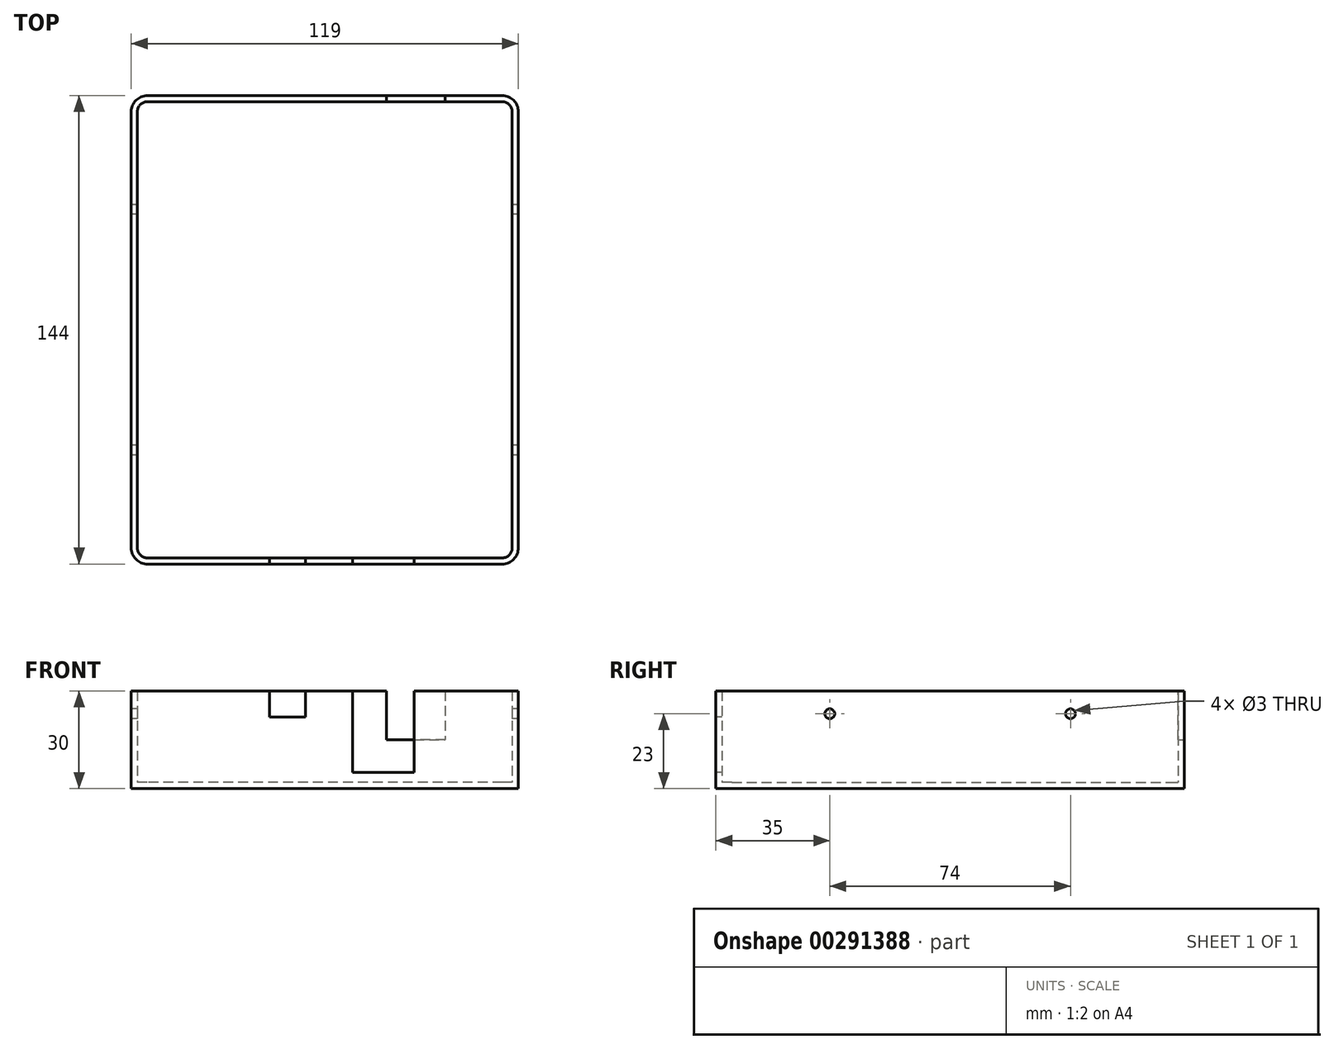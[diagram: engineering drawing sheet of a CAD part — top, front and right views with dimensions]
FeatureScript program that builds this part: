
annotation { "Feature Type Name" : "Feature", "Feature Type Description" : "" }
export const myFeature = defineFeature(function(context is Context, id is Id, definition is map)
    precondition{}
    {
        {
            var Q0;
            Q0=qCreatedBy(makeId("Top.planeOp"),FACE);
            var sketch = newSketch(context, id + "F0", { "sketchPlane" : qUnion([Q0])});
            skLineSegment(sketch, "E0.bottom", {"start": v(59.5, -72) * mm, "end": v(-59.5, -72) * mm});
            skLineSegment(sketch, "E0.top", {"start": v(59.5, 72) * mm, "end": v(-59.5, 72) * mm});
            skLineSegment(sketch, "E0.left", {"start": v(59.5, -72) * mm, "end": v(59.5, 72) * mm});
            skLineSegment(sketch, "E0.right", {"start": v(-59.5, -72) * mm, "end": v(-59.5, 72) * mm});
            skPoint(sketch, "E0.middle", {"position": v(0, 0) * mm});
            skSolve(sketch);
        }
        {
            var Q0;
            Q0 = qSketchRegion(id + "F0", true);
            extrude(context, id + "F1", {"entities" : qUnion([Q0]), "depth" : 30 * mm});
        }
        {
            var Q0;
            Q0=makeQuery(id+"F1.opExtrude","CAP_FACE",FACE,{"disambiguationData":[OSD([sQuery(id+"F0.wireOp",EDGE,"E0.bottom"),sQuery(id+"F0.wireOp",EDGE,"E0.top"),sQuery(id+"F0.wireOp",EDGE,"E0.left"),sQuery(id+"F0.wireOp",EDGE,"E0.right")])],"isStart":false});
            shell(context, id + "F2", {"entities" : qUnion([Q0]), "thickness" : 1.9 * mm});
        }
        {
            var Q0;
            Q0=makeQuery(id+"F1.opExtrude","SWEPT_EDGE",EDGE,{"disambiguationData":[OSD([sQuery(id+"F0.wireOp",EDGE,"E0.bottom"),sQuery(id+"F0.wireOp",EDGE,"E0.right")])]});
            var Q1;
            Q1=makeQuery(id+"F1.opExtrude","SWEPT_EDGE",EDGE,{"disambiguationData":[OSD([sQuery(id+"F0.wireOp",EDGE,"E0.bottom"),sQuery(id+"F0.wireOp",EDGE,"E0.left")])]});
            var Q2;
            Q2=makeQuery(id+"F1.opExtrude","SWEPT_EDGE",EDGE,{"disambiguationData":[OSD([sQuery(id+"F0.wireOp",EDGE,"E0.top"),sQuery(id+"F0.wireOp",EDGE,"E0.left")])]});
            var Q3;
            Q3=makeQuery(id+"F1.opExtrude","SWEPT_EDGE",EDGE,{"disambiguationData":[OSD([sQuery(id+"F0.wireOp",EDGE,"E0.top"),sQuery(id+"F0.wireOp",EDGE,"E0.right")])]});
            fillet(context, id + "F3", {"entities" : qUnion([Q0, Q1, Q2, Q3]), "radius" : 5 * mm, "tangentPropagation" : true, "allowEdgeOverflow" : false});
        }
        {
            var Q0;
            Q0=makeQuery(id+"F2.opShell","OFFSET_EDGE",EDGE,{"disambiguationData":[OSD([sQuery(id+"F0.wireOp",EDGE,"E0.bottom"),sQuery(id+"F0.wireOp",EDGE,"E0.right")])]});
            var Q1;
            Q1=makeQuery(id+"F2.opShell","OFFSET_EDGE",EDGE,{"disambiguationData":[OSD([sQuery(id+"F0.wireOp",EDGE,"E0.bottom"),sQuery(id+"F0.wireOp",EDGE,"E0.left")])]});
            var Q2;
            Q2=makeQuery(id+"F2.opShell","OFFSET_EDGE",EDGE,{"disambiguationData":[OSD([sQuery(id+"F0.wireOp",EDGE,"E0.top"),sQuery(id+"F0.wireOp",EDGE,"E0.right")])]});
            var Q3;
            Q3=makeQuery(id+"F2.opShell","OFFSET_EDGE",EDGE,{"disambiguationData":[OSD([sQuery(id+"F0.wireOp",EDGE,"E0.top"),sQuery(id+"F0.wireOp",EDGE,"E0.left")])]});
            fillet(context, id + "F4", {"entities" : qUnion([Q0, Q1, Q2, Q3]), "radius" : 3 * mm, "tangentPropagation" : true, "allowEdgeOverflow" : false});
        }
        {
            var Q0;
            Q0=makeQuery(id+"F1.opExtrude","SWEPT_FACE",FACE,{"disambiguationData":[OSD([sQuery(id+"F0.wireOp",EDGE,"E0.right")])]});
            var sketch = newSketch(context, id + "F5", { "sketchPlane" : qUnion([Q0])});
            skCircle(sketch, "E1", {"center": v(-37, 23) * mm, "radius": 1.5 * mm});
            skCircle(sketch, "E2", {"center": v(37, 23) * mm, "radius": 1.5 * mm});
            skSolve(sketch);
        }
        {
            var Q0;
            Q0 = qSketchRegion(id + "F5", true);
            extrude(context, id + "F6", {"entities" : qUnion([Q0]), "operationType" : NewBodyOperationType.REMOVE, "endBound" : BoundingType.THROUGH_ALL, "oppositeDirection" : true, "depth" : 25 * mm});
        }
        {
            var Q0;
            Q0=makeQuery(id+"F1.opExtrude","SWEPT_FACE",FACE,{"disambiguationData":[OSD([sQuery(id+"F0.wireOp",EDGE,"E0.bottom")])]});
            var sketch = newSketch(context, id + "F7", { "sketchPlane" : qUnion([Q0])});
            skLineSegment(sketch, "E3.bottom", {"start": v(8.5, 30) * mm, "end": v(27.5, 30) * mm});
            skLineSegment(sketch, "E3.top", {"start": v(8.5, 5) * mm, "end": v(27.5, 5) * mm});
            skLineSegment(sketch, "E3.left", {"start": v(8.5, 30) * mm, "end": v(8.5, 5) * mm});
            skLineSegment(sketch, "E3.right", {"start": v(27.5, 30) * mm, "end": v(27.5, 5) * mm});
            skLineSegment(sketch, "E4.bottom", {"start": v(-17, 30) * mm, "end": v(-6, 30) * mm});
            skLineSegment(sketch, "E4.top", {"start": v(-17, 22) * mm, "end": v(-6, 22) * mm});
            skLineSegment(sketch, "E4.left", {"start": v(-17, 30) * mm, "end": v(-17, 22) * mm});
            skLineSegment(sketch, "E4.right", {"start": v(-6, 30) * mm, "end": v(-6, 22) * mm});
            skSolve(sketch);
        }
        {
            var Q0;
            Q0 = qSketchRegion(id + "F7", true);
            extrude(context, id + "F8", {"entities" : qUnion([Q0]), "operationType" : NewBodyOperationType.REMOVE, "oppositeDirection" : true, "depth" : 3 * mm});
        }
        {
            var Q0;
            Q0=makeQuery(id+"F1.opExtrude","SWEPT_FACE",FACE,{"disambiguationData":[OSD([sQuery(id+"F0.wireOp",EDGE,"E0.top")])]});
            var sketch = newSketch(context, id + "F9", { "sketchPlane" : qUnion([Q0])});
            skLineSegment(sketch, "E5.bottom", {"start": v(-37, 30) * mm, "end": v(-19, 30) * mm});
            skLineSegment(sketch, "E5.top", {"start": v(-37, 15) * mm, "end": v(-19, 15) * mm});
            skLineSegment(sketch, "E5.left", {"start": v(-37, 30) * mm, "end": v(-37, 15) * mm});
            skLineSegment(sketch, "E5.right", {"start": v(-19, 30) * mm, "end": v(-19, 15) * mm});
            skSolve(sketch);
        }
        {
            var Q0;
            Q0 = qSketchRegion(id + "F9", true);
            extrude(context, id + "F10", {"entities" : qUnion([Q0]), "operationType" : NewBodyOperationType.REMOVE, "oppositeDirection" : true, "depth" : 3 * mm});
        }
    });
